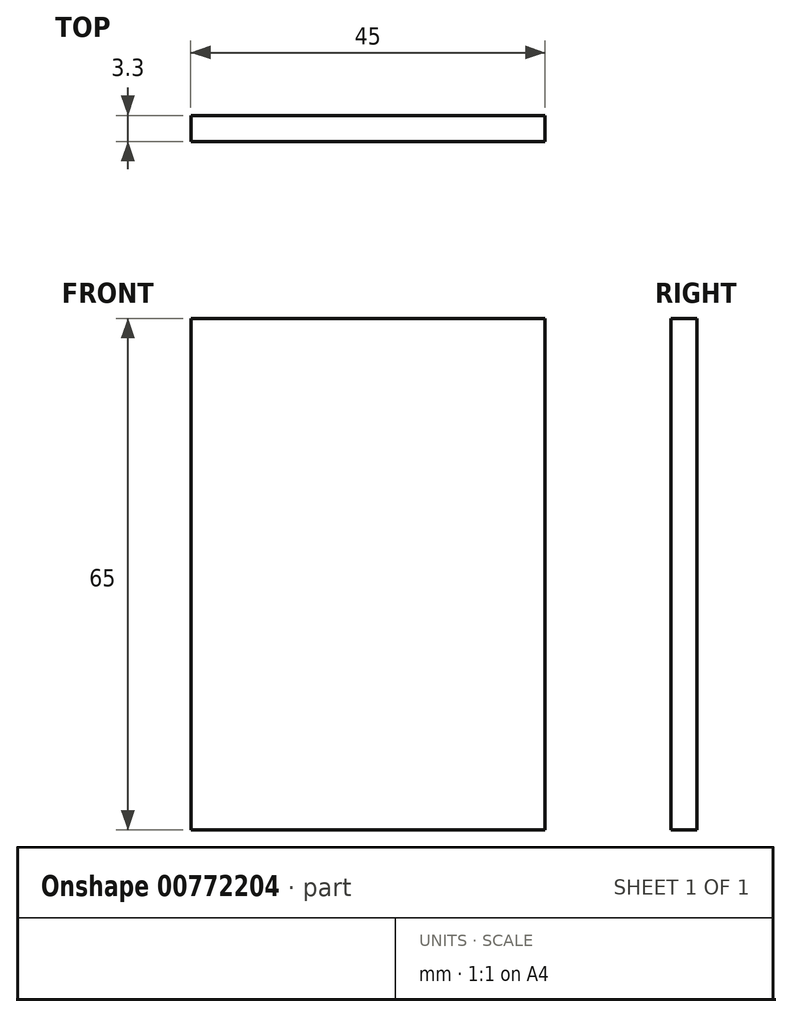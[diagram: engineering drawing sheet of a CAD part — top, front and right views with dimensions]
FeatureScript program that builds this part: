
annotation { "Feature Type Name" : "Feature", "Feature Type Description" : "" }
export const myFeature = defineFeature(function(context is Context, id is Id, definition is map)
    precondition{}
    {
        {
            var Q0;
            Q0=qCreatedBy(makeId("Front.planeOp"),FACE);
            var sketch = newSketch(context, id + "F0", { "sketchPlane" : qUnion([Q0])});
            skLineSegment(sketch, "E0.left", {"start": v(-27.29, 18.4) * mm, "end": v(-27.29, -46.6) * mm});
            skLineSegment(sketch, "E0.right", {"start": v(17.71, 18.4) * mm, "end": v(17.71, -46.6) * mm});
            skLineSegment(sketch, "E1", {"start": v(-27.29, 18.4) * mm, "end": v(17.71, 18.4) * mm});
            skLineSegment(sketch, "E2", {"start": v(-27.29, -46.6) * mm, "end": v(17.71, -46.6) * mm});
            skSolve(sketch);
        }
        {
            var Q0;
            Q0=makeQuery(id+"F0.imprint","IMPRINT",FACE,{"disambiguationData":[TD([[makeQuery(id+"F0.imprint","IMPRINT",EDGE,{"derivedFrom":sQuery(id+"F0.wireOp",EDGE,"E0.left")}),1.0]])]});
            extrude(context, id + "F1", {"entities" : qUnion([Q0]), "depth" : 3.3 * mm, "offsetDistance" : 25 * mm});
        }
    });
